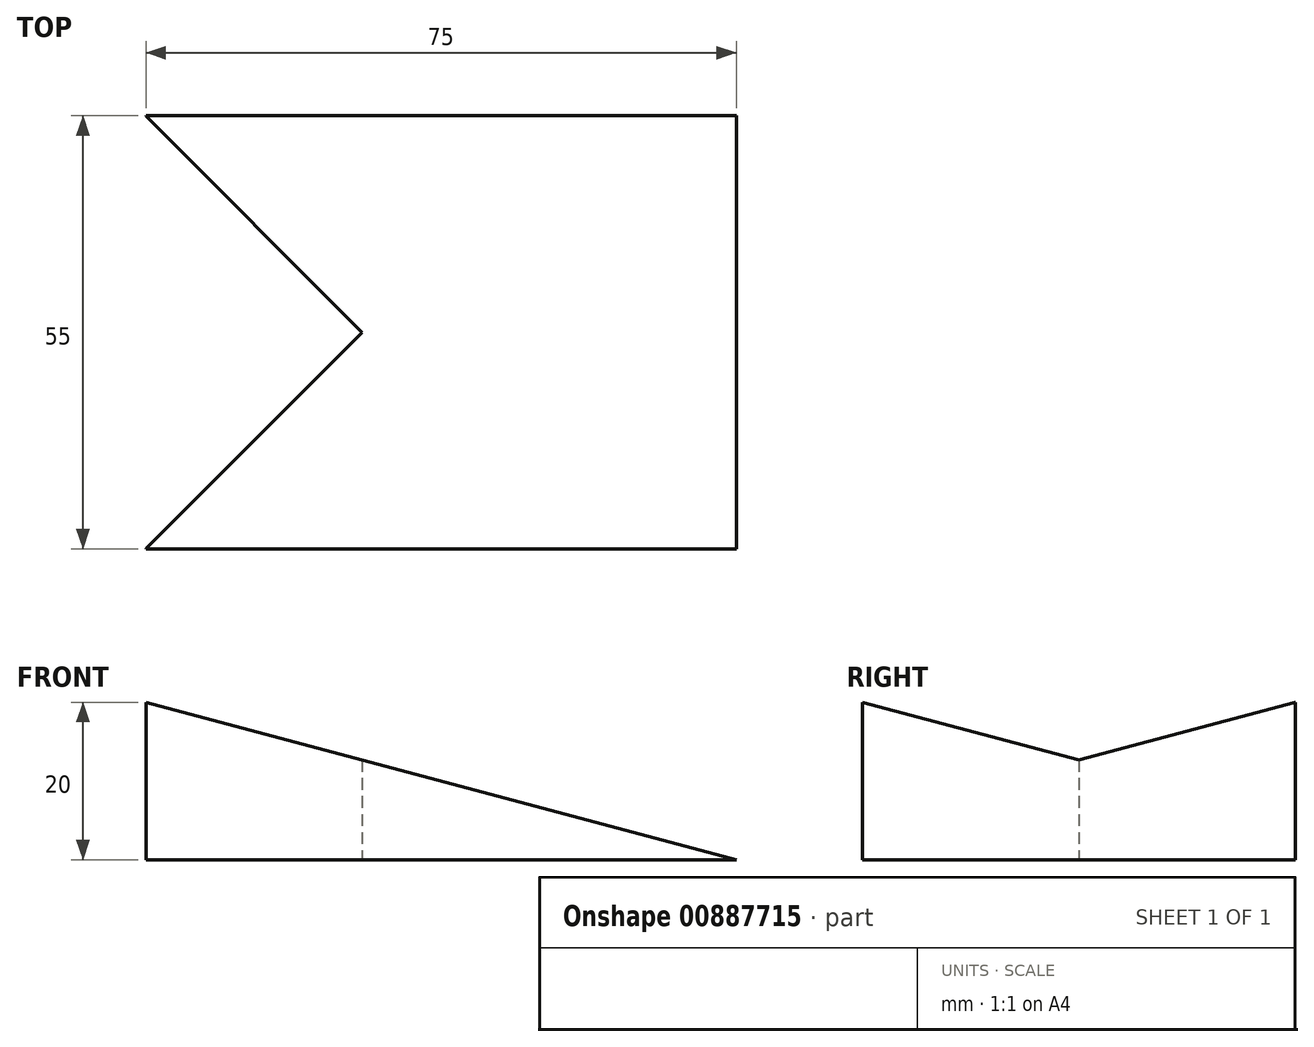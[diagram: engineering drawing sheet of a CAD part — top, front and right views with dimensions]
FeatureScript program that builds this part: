
annotation { "Feature Type Name" : "Feature", "Feature Type Description" : "" }
export const myFeature = defineFeature(function(context is Context, id is Id, definition is map)
    precondition{}
    {
        {
            var Q0;
            Q0=qCreatedBy(makeId("Front.planeOp"),FACE);
            var sketch = newSketch(context, id + "F0", { "sketchPlane" : qUnion([Q0])});
            skLineSegment(sketch, "E0", {"start": v(-22.45, 0) * mm, "end": v(-22.45, 20) * mm});
            skLineSegment(sketch, "E1", {"start": v(-22.45, 20) * mm, "end": v(52.55, 0) * mm});
            skLineSegment(sketch, "E2", {"start": v(52.55, 0) * mm, "end": v(-22.45, 0) * mm});
            skSolve(sketch);
        }
        {
            var Q0;
            Q0=qSketchRegion(id+"F0",true);
            extrude(context, id + "F1", {"entities" : qUnion([Q0]), "depth" : 55 * mm, "offsetDistance" : 25 * mm});
        }
        {
            var Q0;
            Q0=qCreatedBy(makeId("Top.planeOp"),FACE);
            var sketch = newSketch(context, id + "F2", { "sketchPlane" : qUnion([Q0])});
            skLineSegment(sketch, "E3", {"start": v(-22.5, -55) * mm, "end": v(-22.5, 0) * mm});
            skLineSegment(sketch, "E4", {"start": v(-22.5, -55) * mm, "end": v(5, -27.5) * mm});
            skPoint(sketch, "E4.endSnap0", {"position": v(-22.5, -27.5) * mm});
            skLineSegment(sketch, "E5", {"start": v(5, -27.5) * mm, "end": v(-22.5, 0) * mm});
            skSolve(sketch);
        }
        {
            var Q0;
            Q0=qSketchRegion(id+"F2",true);
            extrude(context, id + "F3", {"entities" : qUnion([Q0]), "operationType" : NewBodyOperationType.REMOVE, "depth" : 20 * mm, "offsetDistance" : 25 * mm});
        }
    });
